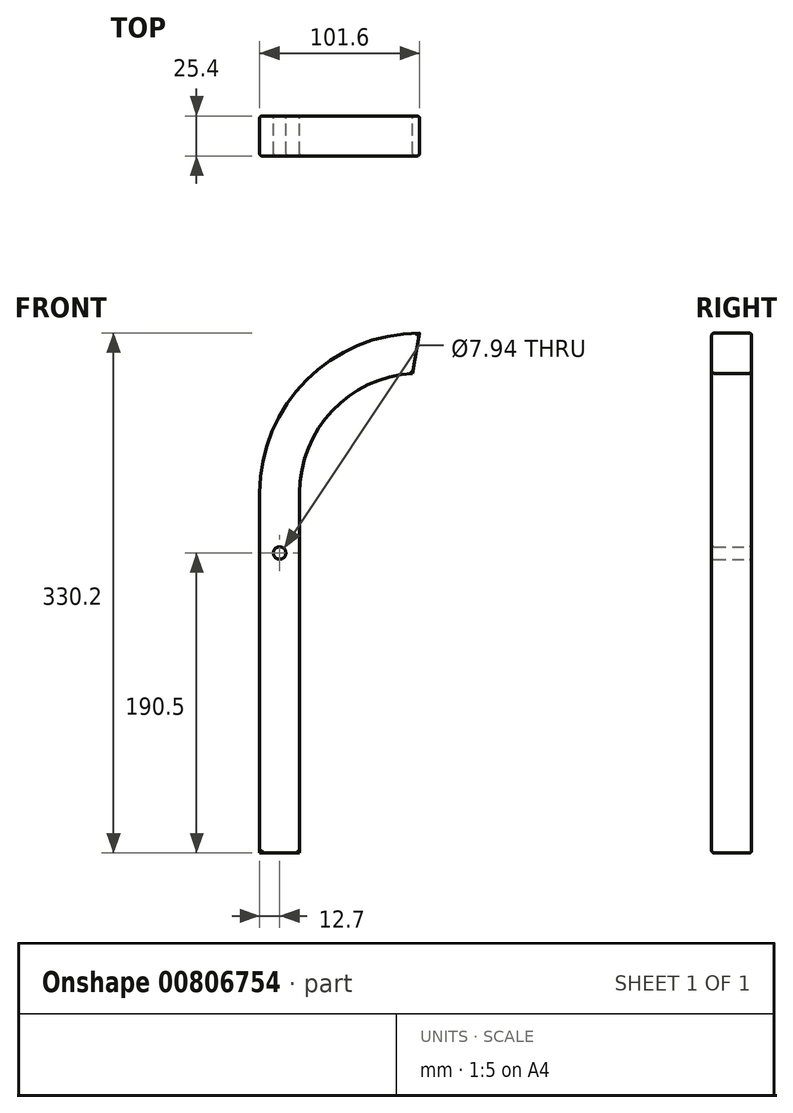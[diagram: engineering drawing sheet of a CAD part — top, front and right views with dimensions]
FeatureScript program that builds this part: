
annotation { "Feature Type Name" : "Feature", "Feature Type Description" : "" }
export const myFeature = defineFeature(function(context is Context, id is Id, definition is map)
    precondition{}
    {
        {
            var Q0;
            Q0=qCreatedBy(makeId("Front.planeOp"),FACE);
            var sketch = newSketch(context, id + "F0", { "sketchPlane" : qUnion([Q0])});
            skLineSegment(sketch, "E0", {"start": v(0, 0) * mm, "end": v(0, 228.6) * mm});
            skLineSegment(sketch, "E1", {"start": v(101.6, 330.2) * mm, "end": v(101.6, 330.2) * mm});
            skPoint(sketch, "E2.visualSharp", {"position": v(0, 330.2) * mm});
            skArc(sketch, "E2.filletArc", {"start": v(101.6, 330.2) * mm, "mid": v(29.76, 300.44) * mm, "end": v(0, 228.6) * mm});
            skArc(sketch, "E3.0", {"start": v(97.1, 304.67) * mm, "mid": v(46.15, 280.87) * mm, "end": v(25.4, 228.6) * mm});
            skLineSegment(sketch, "E3.1", {"start": v(25.4, 0) * mm, "end": v(25.4, 228.6) * mm});
            skLineSegment(sketch, "E4", {"start": v(101.6, 330.2) * mm, "end": v(97.1, 304.67) * mm});
            skLineSegment(sketch, "E5", {"start": v(0, 0) * mm, "end": v(25.4, 0) * mm});
            skCircle(sketch, "E6", {"center": v(12.7, 190.5) * mm, "radius": 3.97 * mm});
            skPoint(sketch, "E6.centerSnap0", {"position": v(12.7, 0) * mm});
            skSolve(sketch);
        }
        {
            var Q0;
            Q0 = qSketchRegion(id + "F0", true);
            extrude(context, id + "F1", {"entities" : qUnion([Q0]), "depth" : 25.4 * mm, "offsetDistance" : 25.4 * mm});
        }
        {
            var Q0;
            Q0=makeQuery(id+"F1.opExtrude","CAP_FACE",FACE,{"disambiguationData":[OSD([sQuery(id+"F0.wireOp",EDGE,"E0"),sQuery(id+"F0.wireOp",EDGE,"E2.filletArc"),sQuery(id+"F0.wireOp",EDGE,"E3.0"),sQuery(id+"F0.wireOp",EDGE,"E3.1"),sQuery(id+"F0.wireOp",EDGE,"E4"),sQuery(id+"F0.wireOp",EDGE,"E5"),sQuery(id+"F0.wireOp",EDGE,"E6")])],"isStart":false});
            var Q1;
            Q1=makeQuery(id+"F1.opExtrude","CAP_FACE",FACE,{"disambiguationData":[OSD([sQuery(id+"F0.wireOp",EDGE,"E0"),sQuery(id+"F0.wireOp",EDGE,"E2.filletArc"),sQuery(id+"F0.wireOp",EDGE,"E3.0"),sQuery(id+"F0.wireOp",EDGE,"E3.1"),sQuery(id+"F0.wireOp",EDGE,"E4"),sQuery(id+"F0.wireOp",EDGE,"E5"),sQuery(id+"F0.wireOp",EDGE,"E6")])],"isStart":true});
            fillet(context, id + "F2", {"entities" : qUnion([Q0, Q1]), "radius" : 1.52 * mm, "tangentPropagation" : true, "allowEdgeOverflow" : false});
        }
    });
